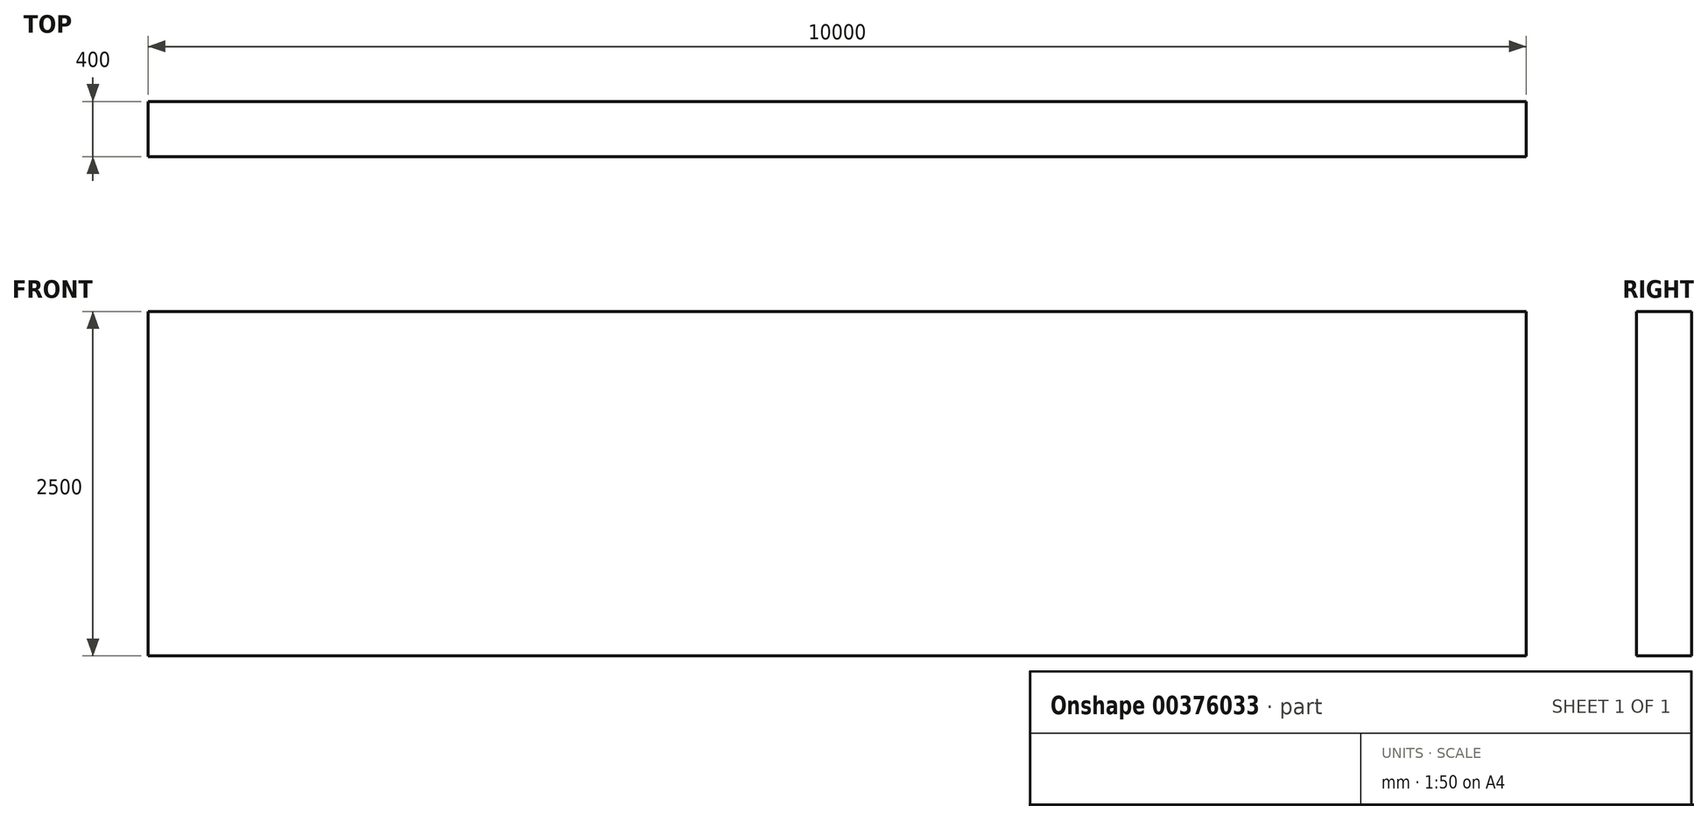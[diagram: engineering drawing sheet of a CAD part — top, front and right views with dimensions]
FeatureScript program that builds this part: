
annotation { "Feature Type Name" : "Feature", "Feature Type Description" : "" }
export const myFeature = defineFeature(function(context is Context, id is Id, definition is map)
    precondition{}
    {
        {
            var Q0;
            Q0=qCreatedBy(makeId("Top.planeOp"),FACE);
            var sketch = newSketch(context, id + "F0", { "sketchPlane" : qUnion([Q0])});
            skLineSegment(sketch, "E0.bottom", {"start": v(-4981.8, -602.46) * mm, "end": v(5018.2, -602.46) * mm});
            skLineSegment(sketch, "E0.top", {"start": v(-4981.8, -202.46) * mm, "end": v(5018.2, -202.46) * mm});
            skLineSegment(sketch, "E0.left", {"start": v(-4981.8, -602.46) * mm, "end": v(-4981.8, -202.46) * mm});
            skLineSegment(sketch, "E0.right", {"start": v(5018.2, -602.46) * mm, "end": v(5018.2, -202.46) * mm});
            skSolve(sketch);
        }
        {
            var Q0;
            Q0=makeQuery(id+"F0.imprint","IMPRINT",FACE,{"disambiguationData":[TD([[makeQuery(id+"F0.imprint","IMPRINT",EDGE,{"derivedFrom":sQuery(id+"F0.wireOp",EDGE,"E0.bottom")}),1.0]])]});
            var Q1;
            Q1=sQuery(id+"F0.wireOp",EDGE,"E0.top");
            var Q2;
            Q2=sQuery(id+"F0.wireOp",EDGE,"E0.bottom");
            extrude(context, id + "F1", {"entities" : qUnion([Q0]), "surfaceEntities" : qUnion([Q1, Q2]), "depth" : 2500 * mm});
        }
    });
